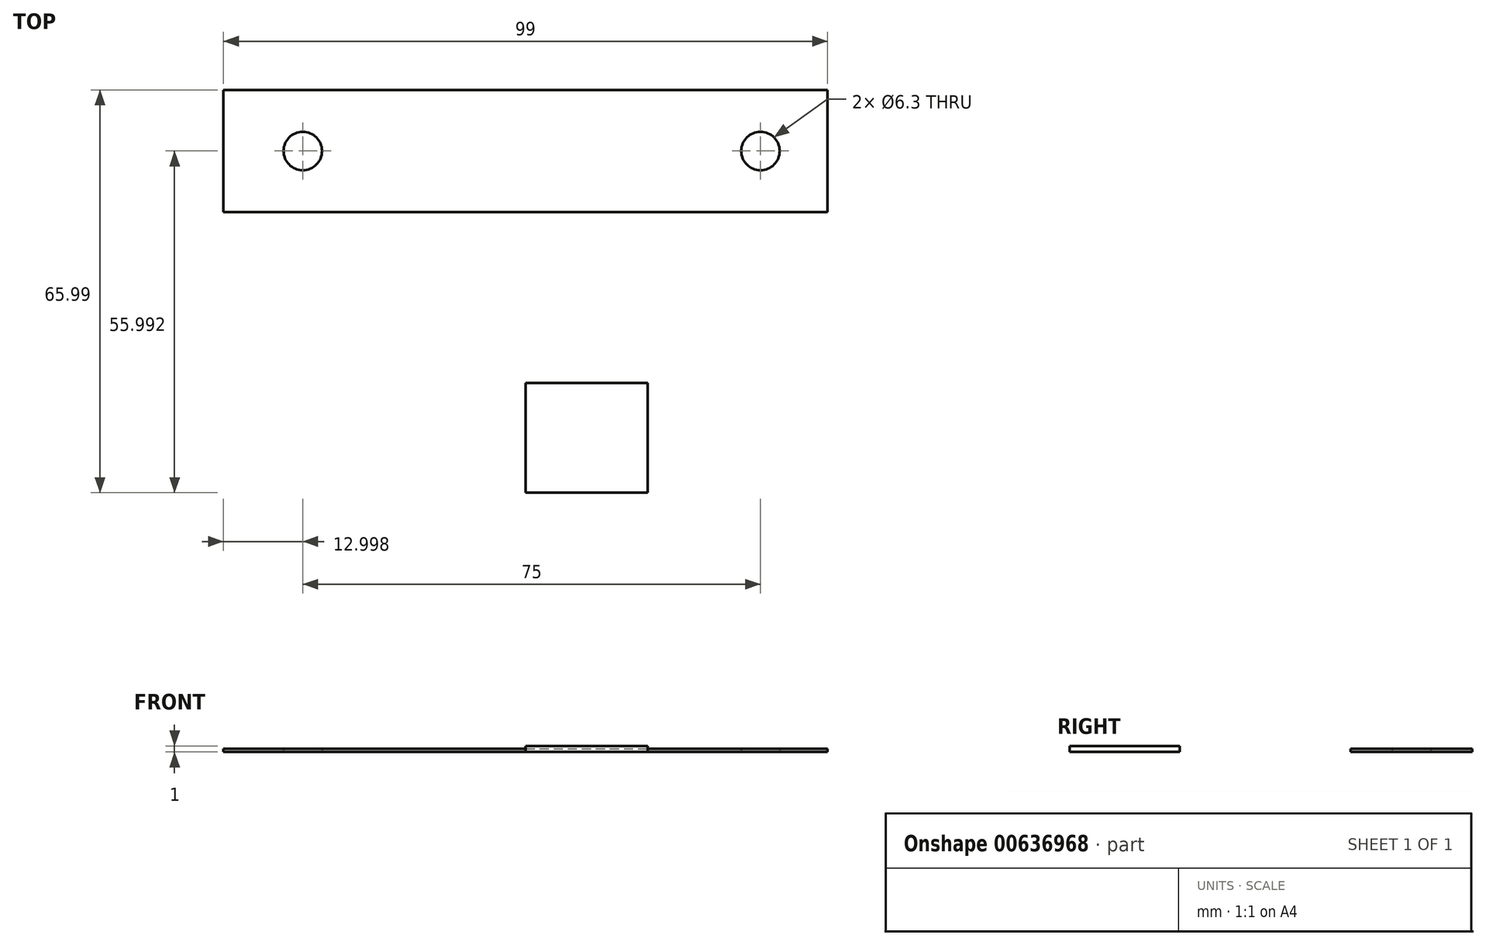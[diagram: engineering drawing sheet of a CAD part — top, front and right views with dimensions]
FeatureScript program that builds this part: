
annotation { "Feature Type Name" : "Feature", "Feature Type Description" : "" }
export const myFeature = defineFeature(function(context is Context, id is Id, definition is map)
    precondition{}
    {
        {
            var Q0;
            Q0=qCreatedBy(makeId("Top.planeOp"),FACE);
            var sketch = newSketch(context, id + "F0", { "sketchPlane" : qUnion([Q0])});
            skLineSegment(sketch, "E0.bottom", {"start": v(-29.91, 40.95) * mm, "end": v(69.09, 40.95) * mm});
            skLineSegment(sketch, "E0.top", {"start": v(-29.91, 20.95) * mm, "end": v(69.09, 20.95) * mm});
            skLineSegment(sketch, "E0.left", {"start": v(-29.91, 40.95) * mm, "end": v(-29.91, 20.95) * mm});
            skLineSegment(sketch, "E0.right", {"start": v(69.09, 40.95) * mm, "end": v(69.09, 20.95) * mm});
            skCircle(sketch, "E1", {"center": v(-16.91, 30.95) * mm, "radius": 3.15 * mm});
            skPoint(sketch, "E2", {"position": v(-29.91, 30.95) * mm});
            skLineSegment(sketch, "E3", {"start": v(19.59, 40.95) * mm, "end": v(19.59, 20.95) * mm, "construction": true});
            skCircle(sketch, "E4.MirrorC", {"center": v(58.09, 30.95) * mm, "radius": 3.15 * mm});
            skLineSegment(sketch, "E5.bottom", {"start": v(19.61, -7.04) * mm, "end": v(39.61, -7.04) * mm});
            skLineSegment(sketch, "E5.top", {"start": v(19.61, -25.04) * mm, "end": v(39.61, -25.04) * mm});
            skLineSegment(sketch, "E5.left", {"start": v(19.61, -7.04) * mm, "end": v(19.61, -25.04) * mm});
            skLineSegment(sketch, "E5.right", {"start": v(39.61, -7.04) * mm, "end": v(39.61, -25.04) * mm});
            skSolve(sketch);
        }
        {
            var Q0;
            Q0=makeQuery(id+"F0.imprint","IMPRINT",FACE,{"disambiguationData":[TD([[makeQuery(id+"F0.imprint","IMPRINT",EDGE,{"derivedFrom":sQuery(id+"F0.wireOp",EDGE,"E0.bottom")}),-1.0]])]});
            extrude(context, id + "F1", {"entities" : qUnion([Q0]), "depth" : 0.5 * mm, "offsetDistance" : 25 * mm});
        }
        {
            var Q0;
            Q0=makeQuery(id+"F0.imprint","IMPRINT",FACE,{"disambiguationData":[TD([[makeQuery(id+"F0.imprint","IMPRINT",EDGE,{"derivedFrom":sQuery(id+"F0.wireOp",EDGE,"E5.bottom")}),-1.0]])]});
            extrude(context, id + "F2", {"entities" : qUnion([Q0]), "depth" : 1 * mm, "offsetDistance" : 25 * mm});
        }
    });
